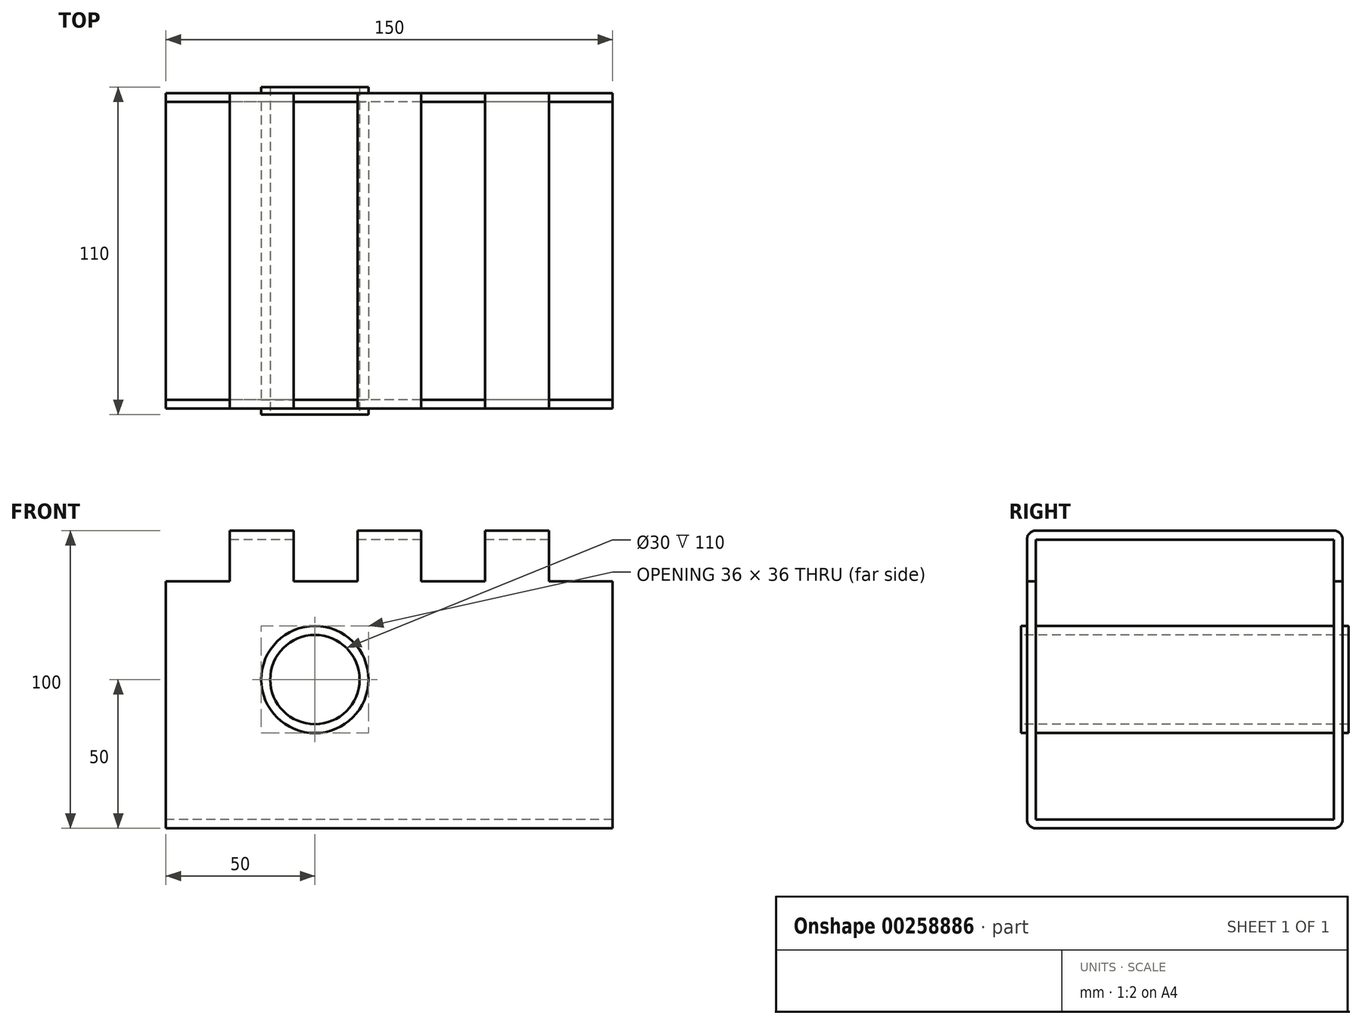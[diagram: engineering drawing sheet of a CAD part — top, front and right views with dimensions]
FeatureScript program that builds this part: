
annotation { "Feature Type Name" : "Feature", "Feature Type Description" : "" }
export const myFeature = defineFeature(function(context is Context, id is Id, definition is map)
    precondition{}
    {
        {
            var Q0;
            Q0=qCreatedBy(makeId("Front.planeOp"),FACE);
            var sketch = newSketch(context, id + "F0", { "sketchPlane" : qUnion([Q0])});
            skLineSegment(sketch, "E0", {"start": v(0, 0) * mm, "end": v(150, 0) * mm});
            skLineSegment(sketch, "E1", {"start": v(150, 0) * mm, "end": v(150, 80) * mm});
            skLineSegment(sketch, "E2", {"start": v(0, 80) * mm, "end": v(0, 0) * mm});
            skCircle(sketch, "E3", {"center": v(50, 47) * mm, "radius": 18 * mm});
            skCircle(sketch, "E4", {"center": v(50, 47) * mm, "radius": 15 * mm});
            skLineSegment(sketch, "E5", {"start": v(0, 0) * mm, "end": v(0, -3) * mm});
            skLineSegment(sketch, "E6", {"start": v(0, -3) * mm, "end": v(150, -3) * mm});
            skLineSegment(sketch, "E7", {"start": v(150, -3) * mm, "end": v(150, 0) * mm});
            skLineSegment(sketch, "E8", {"start": v(0, 80) * mm, "end": v(21.43, 80) * mm});
            skLineSegment(sketch, "E9", {"start": v(21.43, 80) * mm, "end": v(21.43, 103) * mm});
            skLineSegment(sketch, "E10", {"start": v(21.43, 103) * mm, "end": v(42.86, 103) * mm});
            skLineSegment(sketch, "E11", {"start": v(42.86, 103) * mm, "end": v(42.86, 80) * mm});
            skLineSegment(sketch, "E12", {"start": v(42.86, 80) * mm, "end": v(64.29, 80) * mm});
            skLineSegment(sketch, "E13", {"start": v(64.29, 80) * mm, "end": v(64.29, 103) * mm});
            skLineSegment(sketch, "E14", {"start": v(64.29, 103) * mm, "end": v(85.71, 103) * mm});
            skLineSegment(sketch, "E15", {"start": v(85.71, 103) * mm, "end": v(85.71, 80) * mm});
            skLineSegment(sketch, "E16", {"start": v(85.71, 80) * mm, "end": v(107.14, 80) * mm});
            skLineSegment(sketch, "E17", {"start": v(107.14, 80) * mm, "end": v(107.14, 103) * mm});
            skLineSegment(sketch, "E18", {"start": v(107.14, 103) * mm, "end": v(128.57, 103) * mm});
            skLineSegment(sketch, "E19", {"start": v(128.57, 103) * mm, "end": v(128.57, 80) * mm});
            skLineSegment(sketch, "E20", {"start": v(128.57, 80) * mm, "end": v(150, 80) * mm});
            skSolve(sketch);
        }
        {
            var Q0;
            Q0=qCreatedBy(makeId("Right.planeOp"),FACE);
            var sketch = newSketch(context, id + "F1", { "sketchPlane" : qUnion([Q0])});
            skLineSegment(sketch, "E21", {"start": v(0, 0) * mm, "end": v(0, 94) * mm});
            skLineSegment(sketch, "E22", {"start": v(0, 94) * mm, "end": v(100, 94) * mm});
            skLineSegment(sketch, "E23", {"start": v(100, 94) * mm, "end": v(100, 0) * mm});
            skLineSegment(sketch, "E24", {"start": v(100, 0) * mm, "end": v(0, 0) * mm});
            skLineSegment(sketch, "E25.0", {"start": v(0, 97) * mm, "end": v(100, 97) * mm});
            skLineSegment(sketch, "E25.1", {"start": v(-3, 0) * mm, "end": v(-3, 94) * mm});
            skLineSegment(sketch, "E25.2", {"start": v(100, -3) * mm, "end": v(0, -3) * mm});
            skLineSegment(sketch, "E25.3", {"start": v(103, 94) * mm, "end": v(103, 0) * mm});
            skPoint(sketch, "E26.visualSharp", {"position": v(-3, 97) * mm});
            skArc(sketch, "E26.filletArc", {"start": v(0, 97) * mm, "mid": v(-2.12, 96.12) * mm, "end": v(-3, 94) * mm});
            skPoint(sketch, "E27.visualSharp", {"position": v(103, 97) * mm});
            skArc(sketch, "E27.filletArc", {"start": v(103, 94) * mm, "mid": v(102.12, 96.12) * mm, "end": v(100, 97) * mm});
            skPoint(sketch, "E28.visualSharp", {"position": v(103, -3) * mm});
            skArc(sketch, "E28.filletArc", {"start": v(100, -3) * mm, "mid": v(102.12, -2.12) * mm, "end": v(103, 0) * mm});
            skPoint(sketch, "E29.visualSharp", {"position": v(-3, -3) * mm});
            skArc(sketch, "E29.filletArc", {"start": v(-3, 0) * mm, "mid": v(-2.12, -2.12) * mm, "end": v(0, -3) * mm});
            skSolve(sketch);
        }
        {
            var Q0;
            Q0=makeQuery(id+"F0.imprint","IMPRINT",FACE,{"disambiguationData":[TD([[makeQuery(id+"F0.imprint","IMPRINT",EDGE,{"derivedFrom":sQuery(id+"F0.wireOp",EDGE,"E0")}),1.0]])]});
            var Q1;
            Q1=makeQuery(id+"F0.imprint","IMPRINT",FACE,{"disambiguationData":[TD([[makeQuery(id+"F0.imprint","IMPRINT",EDGE,{"derivedFrom":sQuery(id+"F0.wireOp",EDGE,"E0")}),-1.0]])]});
            extrude(context, id + "F2", {"entities" : qUnion([Q0, Q1]), "oppositeDirection" : true, "depth" : 110.5 * mm, "hasSecondDirection" : true, "secondDirectionOppositeDirection" : false, "secondDirectionDepth" : 4.9 * mm});
        }
        {
            var Q0;
            Q0=makeQuery(id+"F1.imprint","IMPRINT",FACE,{"disambiguationData":[TD([[makeQuery(id+"F1.imprint","IMPRINT",EDGE,{"derivedFrom":sQuery(id+"F1.wireOp",EDGE,"E21")}),1.0]])]});
            extrude(context, id + "F3", {"entities" : qUnion([Q0]), "operationType" : NewBodyOperationType.INTERSECT, "depth" : 192.9 * mm});
        }
        {
            var Q0;
            Q0=makeQuery(id+"F0.imprint","IMPRINT",FACE,{"disambiguationData":[TD([[makeQuery(id+"F0.imprint","IMPRINT",EDGE,{"derivedFrom":sQuery(id+"F0.wireOp",EDGE,"E3")}),1.0]])]});
            extrude(context, id + "F4", {"entities" : qUnion([Q0]), "operationType" : NewBodyOperationType.ADD, "oppositeDirection" : true, "depth" : 105 * mm, "hasSecondDirection" : true, "secondDirectionOppositeDirection" : false, "secondDirectionDepth" : 5 * mm});
        }
    });
